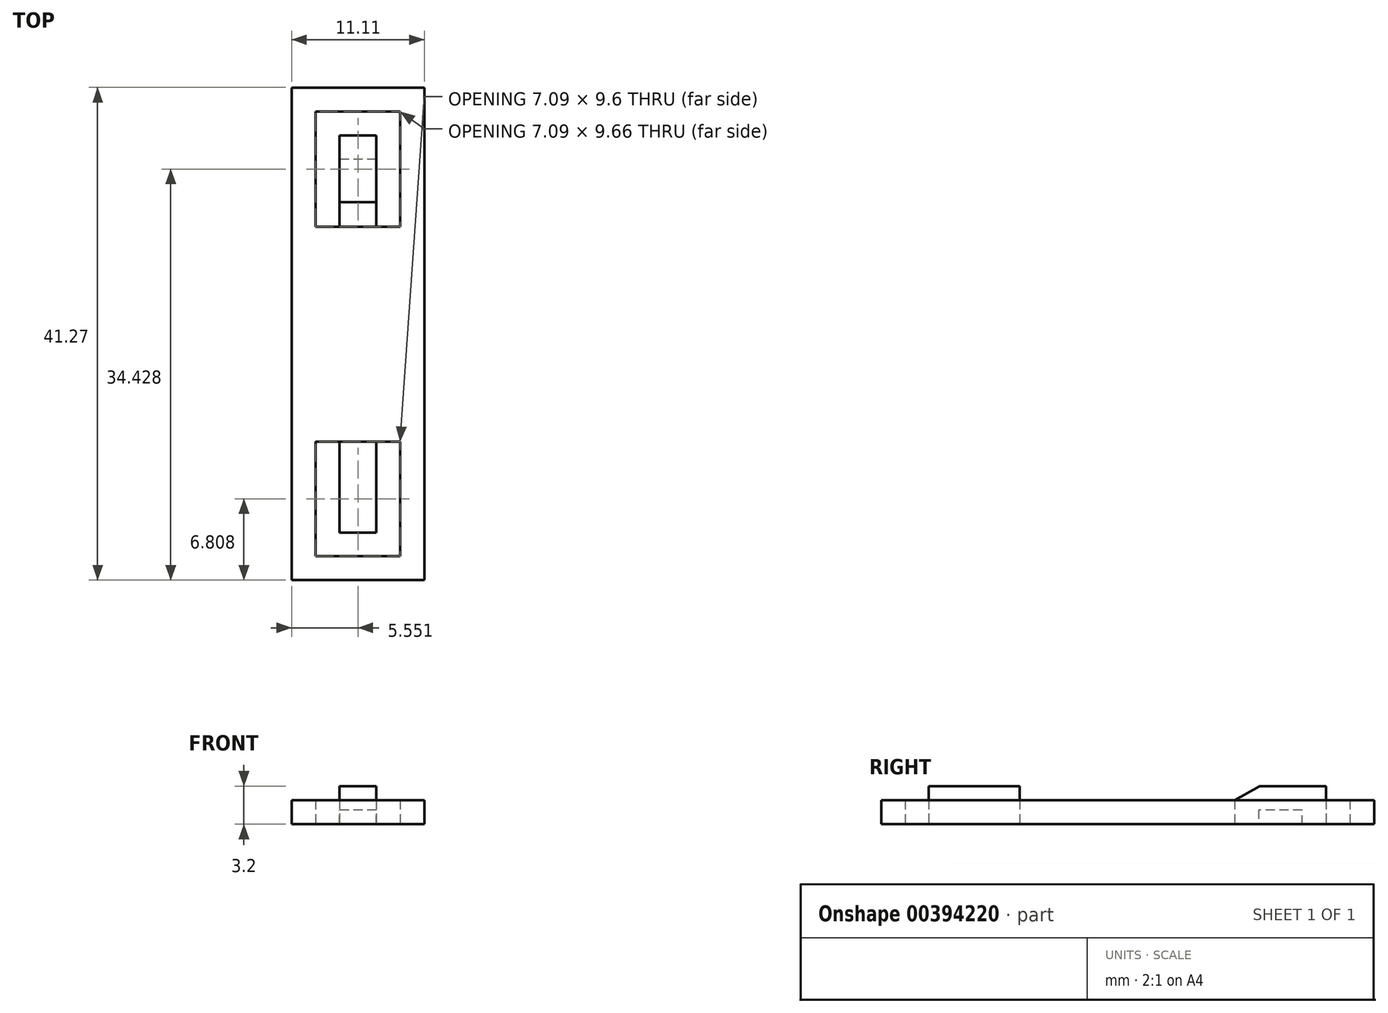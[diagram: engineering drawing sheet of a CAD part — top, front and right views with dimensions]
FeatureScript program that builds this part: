
annotation { "Feature Type Name" : "Feature", "Feature Type Description" : "" }
export const myFeature = defineFeature(function(context is Context, id is Id, definition is map)
    precondition{}
    {
        {
            var Q0;
            Q0=qCreatedBy(makeId("Top.planeOp"),FACE);
            var sketch = newSketch(context, id + "F0", { "sketchPlane" : qUnion([Q0])});
            skLineSegment(sketch, "E0.bottom", {"start": v(-36.94, 49.62) * mm, "end": v(-29.85, 49.62) * mm});
            skLineSegment(sketch, "E0.top", {"start": v(-36.94, 39.96) * mm, "end": v(-34.94, 39.96) * mm});
            skLineSegment(sketch, "E0.left", {"start": v(-36.94, 49.62) * mm, "end": v(-36.94, 39.96) * mm});
            skLineSegment(sketch, "E0.right", {"start": v(-29.85, 49.62) * mm, "end": v(-29.85, 39.96) * mm});
            skLineSegment(sketch, "E1.top", {"start": v(-34.94, 47.61) * mm, "end": v(-31.86, 47.61) * mm});
            skLineSegment(sketch, "E1.left", {"start": v(-34.94, 39.96) * mm, "end": v(-34.94, 47.61) * mm});
            skLineSegment(sketch, "E1.right", {"start": v(-31.86, 39.96) * mm, "end": v(-31.86, 47.61) * mm});
            skLineSegment(sketch, "E2.MirrorCS", {"start": v(-36.94, 12.34) * mm, "end": v(-36.94, 21.97) * mm});
            skLineSegment(sketch, "E3.MirrorCS", {"start": v(-36.94, 12.37) * mm, "end": v(-29.85, 12.37) * mm});
            skLineSegment(sketch, "E4.MirrorCS", {"start": v(-34.94, 14.35) * mm, "end": v(-31.86, 14.35) * mm});
            skLineSegment(sketch, "E5.MirrorCS", {"start": v(-34.94, 21.97) * mm, "end": v(-34.94, 14.35) * mm});
            skLineSegment(sketch, "E6.MirrorCS", {"start": v(-36.94, 21.97) * mm, "end": v(-34.94, 21.97) * mm});
            skLineSegment(sketch, "E7.MirrorCS", {"start": v(-29.85, 12.34) * mm, "end": v(-29.85, 21.97) * mm});
            skLineSegment(sketch, "E8.MirrorCS", {"start": v(-31.86, 21.97) * mm, "end": v(-31.86, 14.35) * mm});
            skLineSegment(sketch, "E9.trimOffspring", {"start": v(-31.86, 39.96) * mm, "end": v(-29.85, 39.96) * mm});
            skLineSegment(sketch, "E10.trimOffspring", {"start": v(-31.86, 21.97) * mm, "end": v(-29.85, 21.97) * mm});
            skLineSegment(sketch, "E11.bottom", {"start": v(-38.95, 51.63) * mm, "end": v(-27.84, 51.63) * mm});
            skLineSegment(sketch, "E11.top", {"start": v(-38.95, 10.36) * mm, "end": v(-33.4, 10.36) * mm});
            skLineSegment(sketch, "E11.left", {"start": v(-38.95, 51.63) * mm, "end": v(-38.95, 10.36) * mm});
            skLineSegment(sketch, "E11.right", {"start": v(-27.84, 51.63) * mm, "end": v(-27.84, 10.36) * mm});
            skLineSegment(sketch, "E12", {"start": v(-33.4, 51.63) * mm, "end": v(-33.4, 10.36) * mm, "construction": true});
            skLineSegment(sketch, "E13", {"start": v(-38.95, 31) * mm, "end": v(-27.84, 31) * mm, "construction": true});
            skLineSegment(sketch, "E14.trimOffspring", {"start": v(-33.4, 10.36) * mm, "end": v(-27.84, 10.36) * mm});
            skLineSegment(sketch, "E15", {"start": v(-34.94, 39.96) * mm, "end": v(-31.86, 39.96) * mm});
            skLineSegment(sketch, "E16", {"start": v(-34.94, 21.97) * mm, "end": v(-31.86, 21.97) * mm});
            skSolve(sketch);
        }
        {
            var Q0;
            Q0 = qSketchRegion(id + "F0", true);
            var Q1;
            Q1=makeQuery(id+"F0.imprint","IMPRINT",FACE,{"disambiguationData":[TD([[makeQuery(id+"F0.imprint","IMPRINT",EDGE,{"derivedFrom":sQuery(id+"F0.wireOp",EDGE,"E4.MirrorCS")}),1.0]])]});
            var Q2;
            Q2=makeQuery(id+"F0.imprint","IMPRINT",FACE,{"disambiguationData":[TD([[makeQuery(id+"F0.imprint","IMPRINT",EDGE,{"derivedFrom":sQuery(id+"F0.wireOp",EDGE,"E1.top")}),-1.0]])]});
            extrude(context, id + "F1", {"entities" : qUnion([Q0, Q1, Q2]), "depth" : 2 * mm, "offsetDistance" : 25 * mm});
        }
        {
            var Q0;
            Q0=makeQuery(id+"F0.imprint","IMPRINT",FACE,{"disambiguationData":[TD([[makeQuery(id+"F0.imprint","IMPRINT",EDGE,{"derivedFrom":sQuery(id+"F0.wireOp",EDGE,"E1.top")}),-1.0]])]});
            var Q1;
            Q1=makeQuery(id+"F0.imprint","IMPRINT",FACE,{"disambiguationData":[TD([[makeQuery(id+"F0.imprint","IMPRINT",EDGE,{"derivedFrom":sQuery(id+"F0.wireOp",EDGE,"E4.MirrorCS")}),1.0]])]});
            extrude(context, id + "F2", {"entities" : qUnion([Q0, Q1]), "operationType" : NewBodyOperationType.ADD, "depth" : 3.2 * mm, "offsetDistance" : 25 * mm});
        }
        {
            var Q0;
            {var subQ0=sQuery(id+"F0.wireOp",EDGE,"E1.left");Q0=makeQuery(id+"F2.boolean.opBoolean","MERGE",FACE,{"derivedFrom":[makeQuery(id+"F1.opExtrude","SWEPT_FACE",FACE,{"disambiguationData":[OSD([subQ0])]}),makeQuery(id+"F2.opExtrude","SWEPT_FACE",FACE,{"disambiguationData":[OSD([subQ0])]})]});}
            var sketch = newSketch(context, id + "F3", { "sketchPlane" : qUnion([Q0])});
            skLineSegment(sketch, "E17", {"start": v(-45.61, 0) * mm, "end": v(-45.61, 1.2) * mm});
            skLineSegment(sketch, "E18", {"start": v(-45.61, 1.2) * mm, "end": v(-41.96, 1.2) * mm});
            skLineSegment(sketch, "E19", {"start": v(-41.96, 1.2) * mm, "end": v(-41.96, 0) * mm});
            skLineSegment(sketch, "E20", {"start": v(-39.96, 2) * mm, "end": v(-42.04, 3.2) * mm});
            skSolve(sketch);
        }
        {
            var Q0;
            {var subQ0=sQuery(id+"F3.wireOp",EDGE,"E17");Q0=makeQuery(id+"F3.imprint","IMPRINT",FACE,{"disambiguationData":[TD([[makeQuery(id+"F3.imprint","IMPRINT",EDGE,{"derivedFrom":subQ0}),-1.0]])]});}
            extrude(context, id + "F4", {"entities" : qUnion([Q0]), "operationType" : NewBodyOperationType.REMOVE, "endBound" : BoundingType.UP_TO_NEXT, "oppositeDirection" : true, "depth" : 25 * mm, "offsetDistance" : 25 * mm});
        }
        {
            var Q0;
            {var subQ0=sQuery(id+"F3.wireOp",EDGE,"E20");Q0=makeQuery(id+"F3.imprint","IMPRINT",FACE,{"disambiguationData":[TD([[makeQuery(id+"F3.imprint","IMPRINT",EDGE,{"derivedFrom":subQ0}),-1.0]])]});}
            extrude(context, id + "F5", {"entities" : qUnion([Q0]), "operationType" : NewBodyOperationType.REMOVE, "oppositeDirection" : true, "depth" : 25 * mm, "offsetDistance" : 25 * mm});
        }
    });
